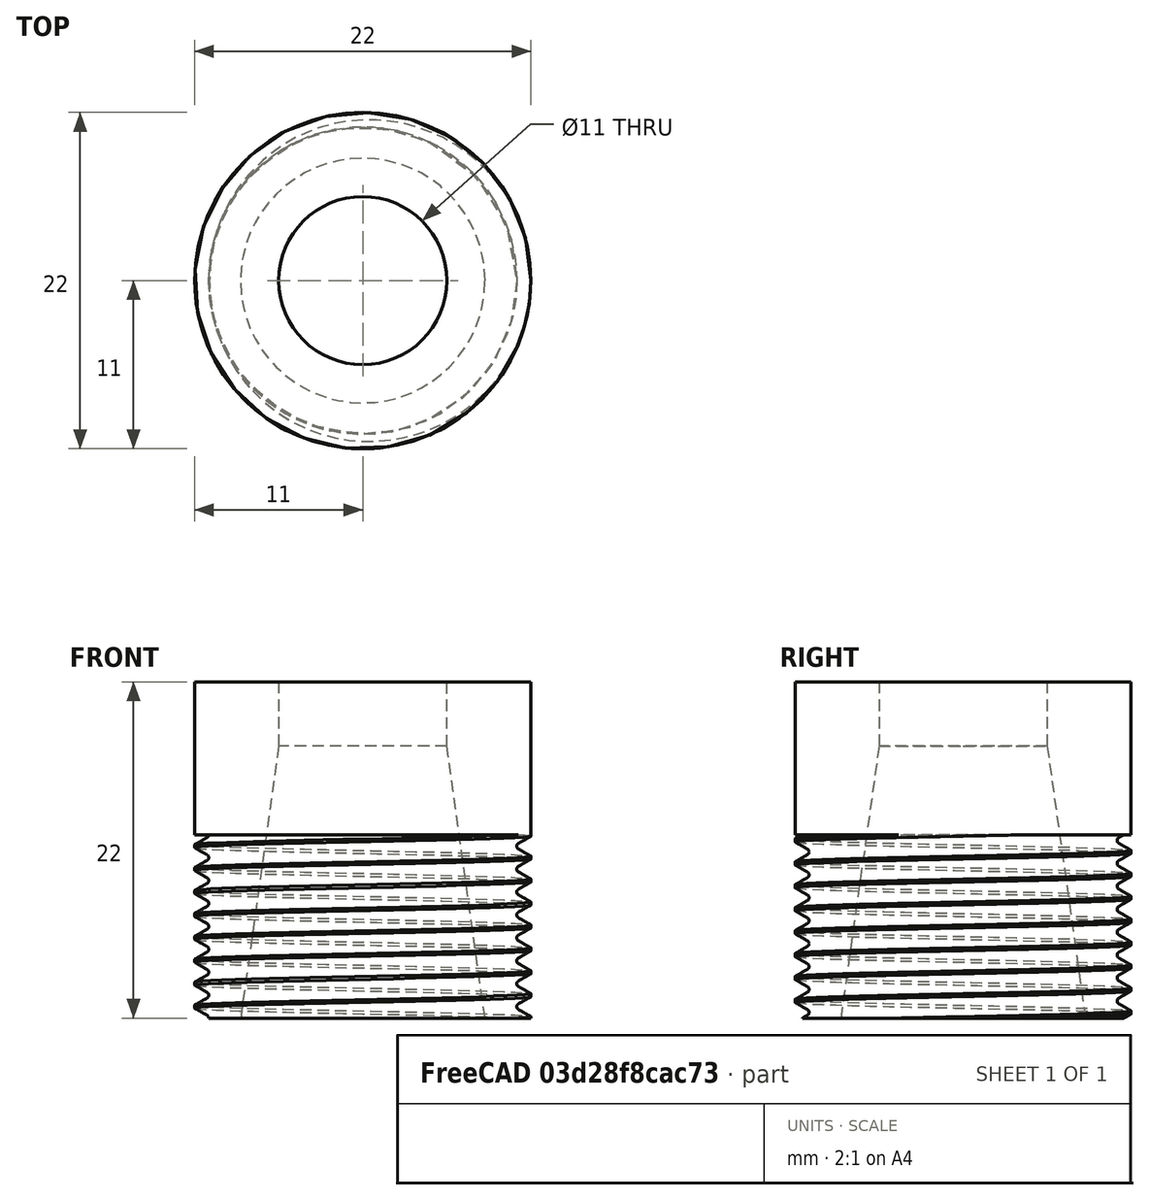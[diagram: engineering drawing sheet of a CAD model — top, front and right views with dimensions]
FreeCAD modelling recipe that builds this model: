
FCSTD DOCUMENT  (FreeCAD 1.0R1.0rc2)
Label: ERSeat
License: All rights reserved
LicenseURL: http://en.wikipedia.org/wiki/All_rights_reserved
objects: Part::Cut×3, Part::Cylinder×2, Spreadsheet::Sheet×1, Part::Cone×1, Part::FeaturePython×1
note: 7 computed .brp shape members not serialized (recipe doc carries the construction recipe); baked Part::Feature solids carry a one-line shape summary decoded from their .brp

FEATURE [Spreadsheet::Sheet] Spreadsheet  label="ERConfigurationTable"
  cells = A1='ER Variant; B1='Taper Outer Diameter; C1='Bore Diameter; D1='Minimum Bore Length; E1='Thread Diameter; F1='Thread Pitch; G1='Thread Length; A2==hiddenref(Cut002.ER.String); B2(taperOuterDiameter)==.B4; C2(boreDiameter)==.C4; D2(minBoreLength)==.D4; E2(threadDia)==.E4; F2(threadPitch)==.F4; G2(threadLength)==.G4; A3='ER11; B3=11; C3=8; D3=17; E3=14; F3=0.75; G3=8; A4='ER16; B4=16; C4=11; D4=22; E4=22; F4=1.5; G4=12; A5='ER20; B5=20; C5=14; D5=27; E5=25; F5=1.5; G5=13; A6='ER25; B6=25; C6=18; D6=37; E6=32; F6=1.5; G6=13; A7='ER32; B7=32; C7=24; D7=42; E7=40; F7=1.5; G7=15; A8='ER40; B8=40; C8=31; D8=47; E8=50; F8=1.5; G8=16
  expr: .cells.Bind.B2.ZZ2 = tuple(.cells; <<B>> + str(hiddenref(Cut002.ER) + 3); <<ZZ>> + str(hiddenref(Cut002.ER) + 3))
FEATURE [Part::Cylinder] Cylinder
  Angle = 360
  AttacherType = Attacher::AttachEngine3D
  FirstAngle = 0
  Height = 22
  Radius = 11
  SecondAngle = 0
  expr: Height = <<ERConfigurationTable>>.minBoreLength
  expr: Radius = <<ERConfigurationTable>>.threadDia / 2
FEATURE [Part::Cylinder] Cylinder001
  Angle = 360
  AttacherType = Attacher::AttachEngine3D
  FirstAngle = 0
  Height = 22
  Radius = 5.5
  SecondAngle = 0
  expr: Height = <<ERConfigurationTable>>.minBoreLength
  expr: Radius = <<ERConfigurationTable>>.boreDiameter / 2
FEATURE [Part::Cut] Cut
  Base = -> Cylinder
  Tool = -> Cylinder001
FEATURE [Part::Cone] Cone
  Angle = 360
  AttacherType = Attacher::AttachEngine3D
  Height = 17.7884
  Radius1 = 8
  Radius2 = 5.5
  expr: Height = (<<ERConfigurationTable>>.taperOuterDiameter - <<ERConfigurationTable>>.boreDiameter) / 2 / tan(8)
  expr: Radius1 = <<ERConfigurationTable>>.taperOuterDiameter / 2
  expr: Radius2 = <<ERConfigurationTable>>.boreDiameter / 2
FEATURE [Part::Cut] Cut001
  Base = -> Cut
  Tool = -> Cone
FEATURE [Part::FeaturePython] ScrewDie  label="22x12-ScrewDie"  # WARN: FeaturePython — macro-defined, semantics opaque (R4)
  Diameter = 29
  DiameterCustom = 22
  Invert = false
  LeftHanded = false
  Length = 12
  MatchOuter = false
  OffsetAngle = 0
  PitchCustom = 1.5
  Placement = pos=(0,0,12) rot=(0,0,1;0rad)
  Thread = true
  Type = 0
  expr: .Placement.Base.z = <<ERConfigurationTable>>.threadLength
  expr: DiameterCustom = <<ERConfigurationTable>>.threadDia
  expr: Length = <<ERConfigurationTable>>.threadLength
  expr: PitchCustom = <<ERConfigurationTable>>.threadPitch
FEATURE [Part::Cut] Cut002  label="ERColletSeat"
  Base = -> Cut001
  ER = 1
  Tool = -> ScrewDie
  expr: .ER.Enum = Spreadsheet.cells[<<A3:|>>]
